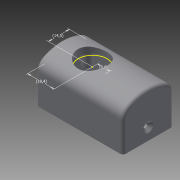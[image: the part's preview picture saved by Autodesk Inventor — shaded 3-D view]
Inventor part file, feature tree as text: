
AUTODESK INVENTOR PART (.ipt)
format: ipt  version: 2014 (Build 180170000, 170)  size: 238,080 bytes
history: native  units: mm
features: sketch x8, extrude x7, projected_geometry x4, fillet x2, chamfer x1
ambient origin geometry x8: Origin, YZ Plane, XZ Plane, XY Plane, X Axis, Y Axis, Z Axis, Center Point
bodies: Solid1 (feature_tree)
feature tree (22):
  extrude  "Extrusion1"  Depth=60.0mm
  extrude  "Extrusion2"  Depth=3.0mm
  fillet  "Fillet1"  Radius=25.0mm
  extrude  "Extrusion3"  Depth=9.0mm
  fillet  "Fillet2"  Radius=20.0mm
  extrude  "Extrusion4"  Depth=2.0mm
  extrude  "Extrusion5"  Depth=2.0mm
  extrude  "Extrusion6"  Depth=2.5mm
  chamfer  "Chamfer1"  Distance=2.5mm
  sketch  "Sketch7"  dims[d19=2.5mm d20=6.0mm d21=2.5mm d22=6.0mm d23=3.0mm]
  extrude  "Extrusion7"  Depth=2.5mm
  sketch  "Sketch1"  dims[d0=60.0mm d1=35.0mm]
  sketch  "Sketch2"  dims[d2=3.0mm d3=3.0mm d4=25.0mm d5=0.0mm]
  sketch  "Sketch3"  dims[d6=25.0mm d7=0.0mm d8=9.0mm d9=20.0mm]
  sketch  "Sketch4"  dims[d10=25.0mm d11=0.0mm d12=2.0mm]
  projected_geometry  "Projected Loop1"
  sketch  "Sketch5"  dims[d13=2.0mm d14=2.0mm]
  projected_geometry  "Projected Loop2"
  projected_geometry  "Projected Loop3"
  projected_geometry  "Projected Loop4"
  sketch  "Sketch6"  dims[d15=2.5mm d16=6.0mm d17=2.5mm d18=6.0mm]
  sketch  "Sketch8"  dims[d24=3.0mm d25=3.0mm d26=3.0mm d27=3.0mm d28=3.0mm d29=3.0mm d30=3.0mm d31=10.0mm d32=0.0mm d33=3.0mm d34=0.0mm d35=3.0mm d36=3.0mm d37=0.0mm d38=2.0mm d39=2.0mm d40=45.0deg d41=18.4mm d42=14.5mm d43=18.4mm d44=8.6mm d45=8.2mm d46=23.0mm d47=2.0mm d48=0.0mm]
